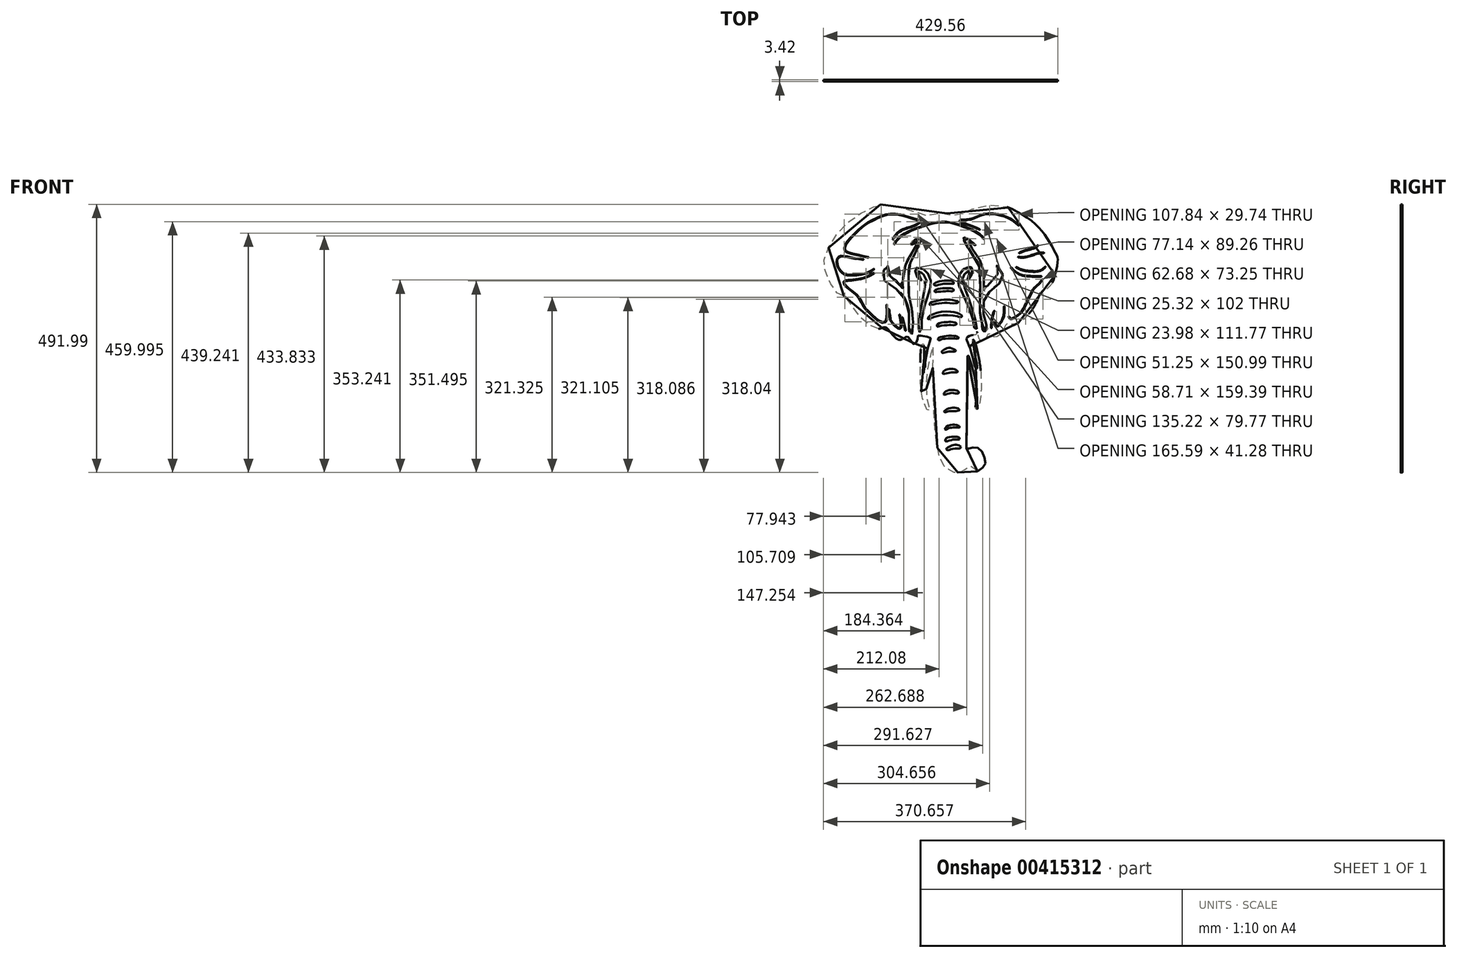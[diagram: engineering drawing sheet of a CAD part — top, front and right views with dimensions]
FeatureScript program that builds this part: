
annotation { "Feature Type Name" : "Feature", "Feature Type Description" : "" }
export const myFeature = defineFeature(function(context is Context, id is Id, definition is map)
    precondition{}
    {
        {
            var Q0;
            Q0=qCreatedBy(makeId("Front.planeOp"),FACE);
            var sketch = newSketch(context, id + "F0", { "sketchPlane" : qUnion([Q0])});
            skLineSegment(sketch, "E0.bottom", {"start": v(-254, 304.8) * mm, "end": v(254, 304.8) * mm, "construction": true});
            skLineSegment(sketch, "E0.top", {"start": v(-254, -304.8) * mm, "end": v(254, -304.8) * mm, "construction": true});
            skLineSegment(sketch, "E0.left", {"start": v(-254, 304.8) * mm, "end": v(-254, -304.8) * mm, "construction": true});
            skLineSegment(sketch, "E0.right", {"start": v(254, 304.8) * mm, "end": v(254, -304.8) * mm, "construction": true});
            skPoint(sketch, "E0.middle", {"position": v(0, 0) * mm});
            skFitSpline(sketch, "E1", {"points": [v(61.1, -298.65) * mm, v(58.43, -299.03) * mm, v(56.48, -297.46) * mm, v(55.38, -295.06) * mm, v(54.47, -292.78) * mm, v(53.43, -290.7) * mm, v(52.38, -289.33) * mm, v(49.59, -289.14) * mm, v(47.05, -290.05) * mm, v(44.58, -291.6) * mm, v(41, -293.95) * mm, v(37.1, -296.1) * mm, v(33.59, -297.79) * mm, v(31.57, -299.42) * mm, v(28.58, -300.46) * mm, v(24.8, -300.85) * mm, v(21.3, -300.85) * mm, v(18.56, -300.85) * mm, v(15.63, -299.35) * mm, v(12.77, -297.79) * mm, v(9.65, -295.9) * mm, v(6.07, -294.28) * mm, v(3.34, -292.46) * mm, v(1.71, -290.96) * mm, v(-1.44, -287.27) * mm, v(-6.48, -278.41) * mm, v(-10.96, -263.1) * mm, v(-13.8, -245.37) * mm, v(-15.64, -231.32) * mm, v(-18.25, -203.48) * mm, v(-19.03, -170.43) * mm, v(-20.63, -121.13) * mm, v(-20, -70.07) * mm, v(-20.33, -69.32) * mm, v(-21.37, -70.2) * mm, v(-22.67, -74.3) * mm, v(-26.44, -93.4) * mm, v(-30.85, -112.34) * mm, v(-33.09, -141.08) * mm, v(-32.47, -156.55) * mm, v(-30.92, -171.1) * mm, v(-26.28, -186.26) * mm, v(-26.21, -189.44) * mm, v(-27.85, -190.32) * mm, v(-29.93, -188.24) * mm, v(-32.77, -182.66) * mm, v(-39.01, -167.89) * mm, v(-42.3, -151.8) * mm, v(-43.94, -115.29) * mm, v(-43.16, -80.94) * mm, v(-40.04, -65.6) * mm, v(-37.95, -65.33) * mm, v(-36.91, -70.02) * mm, v(-36.91, -80.42) * mm, v(-36.91, -96.56) * mm, v(-37.95, -104.62) * mm, v(-39, -112.43) * mm, v(-39, -117.11) * mm, v(-37.7, -117.9) * mm, v(-36.4, -116.6) * mm, v(-36.65, -107.74) * mm, v(-35.1, -108.26) * mm, v(-34.83, -102.8) * mm, v(-33.27, -91.61) * mm, v(-29.63, -72.1) * mm, v(-24.95, -57.27) * mm, v(-24.72, -54.18) * mm, v(-29.1, -52.43) * mm, v(-43.32, -49.47) * mm, v(-47.15, -49.14) * mm, v(-48.57, -51.88) * mm, v(-48.46, -56.7) * mm, v(-50.54, -61.18) * mm, v(-54.04, -65.23) * mm, v(-56.77, -64.68) * mm, v(-61.15, -59.2) * mm, v(-65.75, -52.64) * mm, v(-67.28, -51) * mm, v(-70.34, -52.2) * mm, v(-76.36, -56.15) * mm, v(-81.39, -57.68) * mm, v(-87.19, -55.38) * mm, v(-99.63, -42.15) * mm, v(-106.13, -35.12) * mm, v(-110.56, -34.6) * mm, v(-114.72, -36.16) * mm, v(-122.53, -36.94) * mm, v(-131.9, -33.82) * mm, v(-142.3, -26.01) * mm, v(-158.7, -10.92) * mm, v(-168.06, 3.65) * mm, v(-177.17, 17.7) * mm, v(-186.8, 24.98) * mm, v(-195.12, 27.85) * mm, v(-203.19, 35.91) * mm, v(-213.07, 56.99) * mm, v(-220.44, 76.4) * mm, v(-220.48, 87.61) * mm, v(-213.98, 106.6) * mm, v(-202, 129.24) * mm, v(-183.01, 151.62) * mm, v(-160.12, 170.35) * mm, v(-139.04, 181.54) * mm, v(-121.87, 189.6) * mm, v(-109.38, 190.91) * mm, v(-91.16, 188.57) * mm, v(-61.72, 180.88) * mm, v(-34.4, 170.2) * mm, v(-28.41, 172.55) * mm, v(5.42, 174.11) * mm, v(15.82, 170.99) * mm, v(28.57, 174.11) * mm, v(37.42, 175.15) * mm, v(41.06, 178.53) * mm, v(73.07, 187.38) * mm, v(100.85, 190.41) * mm, v(157.08, 163.06) * mm, v(190.43, 126.35) * mm, v(206.4, 97.47) * mm, v(208.37, 87.84) * mm, v(199.26, 49.74) * mm, v(191.53, 38.91) * mm, v(185.03, 33.96) * mm, v(180.36, 33.27) * mm, v(175.16, 25.08) * mm, v(162.8, 0) * mm, v(138.7, -25.04) * mm, v(128.54, -28.94) * mm, v(119.96, -28.42) * mm, v(115.8, -27.38) * mm, v(109.81, -36.48) * mm, v(101.74, -48.71) * mm, v(92.12, -52.36) * mm, v(86.4, -48.45) * mm, v(81.19, -46.63) * mm, v(73.12, -59.9) * mm, v(68.18, -61.2) * mm, v(64.02, -55.22) * mm, v(61.67, -45.07) * mm, v(59.85, -43.25) * mm, v(58.81, -47.15) * mm, v(53.35, -48.71) * mm, v(45.8, -50.8) * mm, v(41.12, -53.92) * mm, v(42.94, -61.72) * mm, v(50.23, -81.24) * mm, v(58.62, -110.2) * mm, v(60.6, -109.77) * mm, v(57.97, -92.04) * mm, v(54.47, -72.57) * mm, v(52.72, -61.55) * mm, v(52.98, -57.13) * mm, v(57.01, -63.5) * mm, v(62.35, -84.45) * mm, v(66.39, -107.43) * mm, v(67.77, -129.06) * mm, v(66.78, -164.72) * mm, v(61.7, -183.07) * mm, v(59.63, -185.02) * mm, v(58.2, -184.5) * mm, v(57.55, -179.3) * mm, v(59.1, -163.03) * mm, v(58.07, -139.74) * mm, v(52.86, -111.51) * mm, v(43.37, -84.97) * mm, v(42.45, -91.22) * mm, v(42.98, -125.3) * mm, v(41.93, -179.55) * mm, v(41.15, -237.32) * mm, v(41.28, -257.35) * mm, v(42.2, -258.26) * mm, v(45.45, -256.83) * mm, v(51.7, -255.14) * mm, v(59.1, -254.75) * mm, v(67.56, -259.43) * mm, v(73.68, -272.05) * mm, v(75.63, -283.9) * mm, v(71.86, -290.66) * mm, v(61.1, -298.65) * mm]});
            skSolve(sketch);
        }
        {
            var Q0;
            Q0 = qSketchRegion(id + "F0", true);
            extrude(context, id + "F1", {"entities" : qUnion([Q0]), "endBound" : BoundingType.SYMMETRIC, "depth" : 3.42 * mm});
        }
        {
            var Q0;
            Q0=qCreatedBy(makeId("Front.planeOp"),FACE);
            var sketch = newSketch(context, id + "F2", { "sketchPlane" : qUnion([Q0])});
            skFitSpline(sketch, "E2", {"points": [v(30.41, -253.7) * mm, v(28.47, -251.76) * mm, v(21.82, -249.72) * mm, v(15.17, -250.74) * mm, v(7.8, -254.01) * mm, v(4.23, -257.39) * mm, v(5.45, -259.74) * mm, v(10.98, -258.62) * mm, v(22.23, -256.77) * mm, v(29.08, -256.47) * mm, v(30.41, -253.7) * mm]});
            skFitSpline(sketch, "E3", {"points": [v(28.06, -239.8) * mm, v(24.38, -240.3) * mm, v(16.4, -240.4) * mm, v(4.53, -243.68) * mm, v(2.18, -242.96) * mm, v(3, -239.08) * mm, v(11.8, -235.5) * mm, v(24.68, -235.4) * mm, v(27.45, -236.83) * mm, v(28.06, -239.8) * mm]});
            skFitSpline(sketch, "E4", {"points": [v(25.81, -218) * mm, v(15.48, -218.52) * mm, v(7.6, -220.05) * mm, v(2.9, -222.5) * mm, v(1.57, -220.15) * mm, v(13.23, -213.2) * mm, v(26.01, -214.83) * mm, v(28.06, -216.47) * mm, v(28.06, -218.41) * mm, v(25.81, -218) * mm]});
            skFitSpline(sketch, "E5", {"points": [v(14.66, -188.44) * mm, v(7.1, -188.65) * mm, v(2.38, -190.28) * mm, v(0, -189.36) * mm, v(1.67, -186.9) * mm, v(12.1, -182.4) * mm, v(24.48, -182.92) * mm, v(28.06, -186.2) * mm, v(25.81, -187.52) * mm, v(14.66, -188.44) * mm]});
            skFitSpline(sketch, "E6", {"points": [v(14.66, -154.79) * mm, v(6.78, -156.32) * mm, v(0, -158.06) * mm, v(-1, -156.52) * mm, v(1.67, -152.84) * mm, v(10.16, -149.47) * mm, v(19.37, -149.77) * mm, v(25.81, -152.02) * mm, v(26.73, -155) * mm, v(22.03, -155.8) * mm, v(14.66, -154.79) * mm]});
            skFitSpline(sketch, "E7", {"points": [v(10.57, -117.55) * mm, v(17.93, -117.04) * mm, v(23.25, -117.24) * mm, v(24.79, -115.6) * mm, v(21.1, -112.33) * mm, v(11.8, -110.8) * mm, v(4.33, -112.23) * mm, v(-1.7, -116.02) * mm, v(-2.42, -119.5) * mm, v(1.36, -119.9) * mm, v(10.57, -117.55) * mm]});
            skFitSpline(sketch, "E8", {"points": [v(8.32, -79.09) * mm, v(14.66, -78.98) * mm, v(19.88, -78.88) * mm, v(21.3, -77.25) * mm, v(17.83, -74.69) * mm, v(9.65, -72.13) * mm, v(2.49, -73.97) * mm, v(-2.22, -77.04) * mm, v(-4.37, -79.09) * mm, v(-3.24, -81.54) * mm, v(1.67, -80.52) * mm, v(8.32, -79.09) * mm]});
            skFitSpline(sketch, "E9", {"points": [v(6.99, -55.05) * mm, v(16.7, -54.74) * mm, v(23.97, -55.35) * mm, v(26.73, -53.82) * mm, v(23.46, -51.26) * mm, v(16.4, -50.14) * mm, v(4.02, -50.34) * mm, v(-3.65, -51.88) * mm, v(-10.5, -54.23) * mm, v(-11.22, -57.2) * mm, v(-8.36, -58.22) * mm, v(-4.06, -56.17) * mm, v(6.99, -55.05) * mm]});
            skFitSpline(sketch, "E10", {"points": [v(5.04, -30.5) * mm, v(13.43, -30.4) * mm, v(21.3, -29.98) * mm, v(22.84, -27.63) * mm, v(19.06, -25.69) * mm, v(9.95, -24.26) * mm, v(4.63, -25.18) * mm, v(-2.22, -25.18) * mm, v(-11.22, -28.45) * mm, v(-12.96, -29.68) * mm, v(-12.86, -33.36) * mm, v(-8.36, -32.24) * mm, v(5.04, -30.5) * mm]});
            skFitSpline(sketch, "E11", {"points": [v(-2.42, -12.6) * mm, v(-12.35, -13.82) * mm, v(-21.25, -16.17) * mm, v(-26.16, -19.14) * mm, v(-29.33, -19.55) * mm, v(-29.63, -16.69) * mm, v(-25.03, -12.8) * mm, v(-9.58, -6.76) * mm, v(12.4, -6.05) * mm, v(22.84, -8) * mm, v(30.41, -11.16) * mm, v(32.87, -14.33) * mm, v(30.41, -16.17) * mm, v(23.46, -14.13) * mm, v(-2.42, -12.6) * mm]});
            skFitSpline(sketch, "E12", {"points": [v(0.75, 10.32) * mm, v(10.06, 10.01) * mm, v(24.38, 10.32) * mm, v(25.81, 12.67) * mm, v(18.85, 14.72) * mm, v(9.55, 16.15) * mm, v(-4.26, 15.64) * mm, v(-18.18, 12.57) * mm, v(-26.05, 9.5) * mm, v(-26.57, 6.53) * mm, v(-21.25, 7.25) * mm, v(-10.5, 9.2) * mm, v(0.75, 10.32) * mm]});
            skFitSpline(sketch, "E13", {"points": [v(1.87, 31.59) * mm, v(9.27, 31.93) * mm, v(16.67, 31.93) * mm, v(17.61, 34.69) * mm, v(11.68, 37.18) * mm, v(4.2, 37.44) * mm, v(-7.33, 36.66) * mm, v(-15.76, 33.83) * mm, v(-17.48, 32.02) * mm, v(-16.7, 30.21) * mm, v(-9.83, 30.73) * mm, v(1.87, 31.59) * mm]});
            skFitSpline(sketch, "E14", {"points": [v(-3.9, 44.75) * mm, v(2.56, 45.52) * mm, v(12.7, 45.27) * mm, v(17.44, 45.78) * mm, v(16.92, 48.97) * mm, v(11.08, 51.12) * mm, v(1.78, 51.29) * mm, v(-9.05, 49.74) * mm, v(-16.97, 46.73) * mm, v(-18.86, 43.55) * mm, v(-16.1, 42.08) * mm, v(-9.48, 43.72) * mm, v(-3.9, 44.75) * mm]});
            skSolve(sketch);
        }
        {
            var Q0;
            Q0 = qSketchRegion(id + "F2", true);
            extrude(context, id + "F3", {"entities" : qUnion([Q0]), "operationType" : NewBodyOperationType.REMOVE, "endBound" : BoundingType.THROUGH_ALL, "oppositeDirection" : true, "depth" : 25.4 * mm, "hasSecondDirection" : true, "secondDirectionBound" : SecondDirectionBoundingType.THROUGH_ALL, "secondDirectionOppositeDirection" : false, "secondDirectionDepth" : 25.4 * mm});
        }
        {
            var Q0;
            Q0=qCreatedBy(makeId("Front.planeOp"),FACE);
            var sketch = newSketch(context, id + "F4", { "sketchPlane" : qUnion([Q0])});
            skFitSpline(sketch, "E15", {"points": [v(-47.27, 69.23) * mm, v(-42.4, 67.65) * mm, v(-36.57, 61.08) * mm, v(-33.28, 54.63) * mm, v(-31.95, 47.58) * mm, v(-32.43, 46.12) * mm, v(-35.47, 47.94) * mm, v(-36.81, 48.43) * mm, v(-37.3, 46.36) * mm, v(-34.99, 43.93) * mm, v(-34.5, 39.91) * mm, v(-36.94, 28.39) * mm, v(-41.18, 8.56) * mm, v(-44.8, -12.77) * mm, v(-46.69, -30.23) * mm, v(-46.52, -40.56) * mm, v(-44.2, -43.57) * mm, v(-41.61, -42.02) * mm, v(-41.1, -35.65) * mm, v(-40.92, -20.86) * mm, v(-34.9, 7.62) * mm, v(-30.52, 21.47) * mm, v(-25.76, 36.95) * mm, v(-24.73, 43.4) * mm, v(-24.9, 52.18) * mm, v(-28.08, 61.04) * mm, v(-30.66, 65.6) * mm, v(-35.91, 70.84) * mm, v(-41.85, 73.43) * mm, v(-50.02, 74.8) * mm, v(-53.2, 74.63) * mm, v(-53.46, 71.36) * mm, v(-52.08, 64.05) * mm, v(-49.76, 57.86) * mm, v(-46.15, 53.21) * mm, v(-42.45, 51.49) * mm, v(-41.76, 52.6) * mm, v(-42.97, 55.1) * mm, v(-45.12, 59.4) * mm, v(-47.27, 63.53) * mm, v(-47.27, 69.23) * mm]});
            skFitSpline(sketch, "E16", {"points": [v(-103.22, 76.95) * mm, v(-103.08, 64.3) * mm, v(-100.7, 61.08) * mm, v(-95.2, 56.77) * mm, v(-85.28, 48.09) * mm, v(-75.66, 36.59) * mm, v(-75.45, 39.48) * mm, v(-75.37, 57.13) * mm, v(-71.4, 77.38) * mm, v(-65.75, 90.55) * mm, v(-61.2, 98.43) * mm, v(-50.06, 117.1) * mm, v(-48.03, 121.36) * mm, v(-48.25, 122.74) * mm, v(-50.42, 122.74) * mm, v(-57.3, 118.18) * mm, v(-60.47, 117.38) * mm, v(-61.49, 118.4) * mm, v(-58.8, 122.6) * mm, v(-52.37, 127.44) * mm, v(-47.45, 129.97) * mm, v(-43.76, 129.97) * mm, v(-41.88, 127.37) * mm, v(-42.9, 122.66) * mm, v(-50.13, 108.13) * mm, v(-57.16, 95.55) * mm, v(-62.28, 83.17) * mm, v(-64.94, 70.69) * mm, v(-65.37, 53.14) * mm, v(-64.76, 22.49) * mm, v(-62.2, 10.93) * mm, v(-58.8, -1.48) * mm, v(-56.98, -11.82) * mm, v(-56.98, -32.99) * mm, v(-57.46, -42.84) * mm, v(-58.92, -46.49) * mm, v(-61.6, -46.85) * mm, v(-63.54, -43.45) * mm, v(-64.4, -36.51) * mm, v(-64.64, -16.8) * mm, v(-64.64, -4.4) * mm, v(-68.65, 10.2) * mm, v(-74.37, 22.6) * mm, v(-86.78, 34.9) * mm, v(-104.9, 46.82) * mm, v(-110.75, 52.54) * mm, v(-113.06, 59.96) * mm, v(-111.48, 68.6) * mm, v(-107.58, 77.35) * mm, v(-104.78, 80.03) * mm, v(-103.22, 76.95) * mm]});
            skFitSpline(sketch, "E17", {"points": [v(28.9, 62.27) * mm, v(33.29, 70.18) * mm, v(38.28, 73.22) * mm, v(44.36, 75.41) * mm, v(49.83, 75.41) * mm, v(51.17, 71.76) * mm, v(51.17, 65.68) * mm, v(48.25, 58.14) * mm, v(44.48, 53.15) * mm, v(42.9, 52.54) * mm, v(42.9, 55.34) * mm, v(45.57, 62.76) * mm, v(47.4, 66.9) * mm, v(46.3, 69.08) * mm, v(43.02, 68.36) * mm, v(38.28, 65.07) * mm, v(35.48, 58.26) * mm, v(32.92, 52.05) * mm, v(33.17, 46.82) * mm, v(35, 45.73) * mm, v(36.7, 47.67) * mm, v(38.76, 47.43) * mm, v(38.03, 44.51) * mm, v(37.42, 39.04) * mm, v(40.47, 30.64) * mm, v(46.55, 13.73) * mm, v(52.02, -2.69) * mm, v(58.47, -24.46) * mm, v(59.93, -36.75) * mm, v(58.23, -37.72) * mm, v(56.28, -37.48) * mm, v(54.46, -32.25) * mm, v(52.14, -18.87) * mm, v(45.82, 0) * mm, v(37.79, 18.84) * mm, v(27.81, 40.86) * mm, v(26.6, 44.15) * mm, v(26.6, 52.9) * mm, v(28.9, 62.27) * mm]});
            skFitSpline(sketch, "E18", {"points": [v(44.88, 127.77) * mm, v(55.7, 119.26) * mm, v(58.26, 116.83) * mm, v(57.17, 115.85) * mm, v(55.1, 116.58) * mm, v(48.29, 120.72) * mm, v(44.52, 123.15) * mm, v(43.66, 121.57) * mm, v(46.7, 115.85) * mm, v(55.95, 103.57) * mm, v(65.32, 89.45) * mm, v(69.82, 79) * mm, v(72.98, 67.2) * mm, v(74.08, 51.13) * mm, v(72.5, 32.89) * mm, v(73.83, 32.89) * mm, v(79.19, 41.52) * mm, v(97.31, 61.08) * mm, v(97.8, 64.15) * mm, v(96.1, 75.22) * mm, v(96.1, 78.75) * mm, v(98.53, 78.14) * mm, v(105.7, 66.22) * mm, v(108.02, 57.46) * mm, v(105.46, 49.07) * mm, v(97.68, 44.32) * mm, v(86.6, 34.95) * mm, v(76.15, 22.67) * mm, v(73.23, 17.56) * mm, v(72, 7.34) * mm, v(71.89, -6.77) * mm, v(73.96, -23.92) * mm, v(77.48, -30.13) * mm, v(79.67, -34.5) * mm, v(78.46, -40.47) * mm, v(73.35, -42.05) * mm, v(70.18, -39.25) * mm, v(69.58, -29.4) * mm, v(68.36, -22.47) * mm, v(66.05, -11.4) * mm, v(65.93, 31.55) * mm, v(64.59, 74.61) * mm, v(60.45, 86.05) * mm, v(47.44, 105.63) * mm, v(37.46, 122.79) * mm, v(35.51, 129.23) * mm, v(37.95, 130.57) * mm, v(44.88, 127.77) * mm]});
            skSolve(sketch);
        }
        {
            var Q0;
            Q0 = qSketchRegion(id + "F4", true);
            extrude(context, id + "F5", {"entities" : qUnion([Q0]), "operationType" : NewBodyOperationType.REMOVE, "endBound" : BoundingType.THROUGH_ALL, "oppositeDirection" : true, "depth" : 25.4 * mm, "hasSecondDirection" : true, "secondDirectionBound" : SecondDirectionBoundingType.THROUGH_ALL, "secondDirectionOppositeDirection" : false, "secondDirectionDepth" : 25.4 * mm});
        }
        {
            var Q0;
            Q0=qCreatedBy(makeId("Front.planeOp"),FACE);
            var sketch = newSketch(context, id + "F6", { "sketchPlane" : qUnion([Q0])});
            skFitSpline(sketch, "E19", {"points": [v(-71.36, -40.3) * mm, v(-77.15, -17) * mm], "startDerivative": vector(-5.79, 23.3) * mm, "endDerivative": vector(-5.79, 23.3) * mm});
            skFitSpline(sketch, "E20", {"points": [v(-82.28, -11.87) * mm, v(-81.56, -35.95) * mm, v(-96.6, -23.15) * mm, v(-98.5, -17.07) * mm, v(-100.97, -1.72) * mm], "startDerivative": vector(22.12, -113.85) * mm, "endDerivative": vector(-12.6, 71.3) * mm});
            skFitSpline(sketch, "E21", {"points": [v(-105.88, 6.26) * mm, v(-106.08, -19.32) * mm, v(-108.94, -24.64) * mm, v(-117.54, -23.82) * mm, v(-139.02, -4.59) * mm, v(-145.98, 2.57) * mm, v(-155.18, 19.76) * mm, v(-167.87, 31.63) * mm, v(-179.32, 41.24) * mm, v(-183.21, 46.36) * mm, v(-183, 49.42) * mm, v(-178.1, 50.65) * mm, v(-168.89, 51.47) * mm, v(-155.8, 53.1) * mm, v(-142.5, 57) * mm, v(-128.58, 63.75) * mm], "startDerivative": vector(12.16, -310.07) * mm, "endDerivative": vector(185.2, 97.32) * mm});
            skFitSpline(sketch, "E22", {"points": [v(-128.58, 71.52) * mm, v(-136.97, 66.4) * mm, v(-155.39, 61.09) * mm, v(-171.75, 60.47) * mm, v(-180.55, 61.09) * mm, v(-187.92, 65.8) * mm, v(-194.46, 74.18) * mm, v(-197.33, 87.68) * mm, v(-192.42, 95.46) * mm, v(-183.42, 96.48) * mm, v(-168.28, 93.41) * mm, v(-148.63, 90.75) * mm], "startDerivative": vector(-90.9, -64.53) * mm, "endDerivative": vector(175.67, -19.14) * mm});
            skFitSpline(sketch, "E23", {"points": [v(-139.02, 94.23) * mm, v(-159.89, 99.14) * mm, v(-176.46, 103.44) * mm, v(-181.17, 106.71) * mm, v(-181.17, 113.87) * mm, v(-175.64, 123.28) * mm, v(-161.73, 138.42) * mm, v(-142.7, 154.59) * mm, v(-122.86, 165.02) * mm, v(-107.1, 170.95) * mm, v(-89.5, 172.59) * mm, v(-70.9, 168.5) * mm, v(-48.59, 161.54) * mm], "startDerivative": vector(-219.91, 52.2) * mm, "endDerivative": vector(230.65, -73.26) * mm});
            skFitSpline(sketch, "E24", {"points": [v(-43.27, 157.65) * mm, v(-57.39, 150.08) * mm, v(-74.57, 144.36) * mm, v(-87.26, 135.56) * mm, v(-92.99, 126.76) * mm], "startDerivative": vector(-51.9, -32.23) * mm, "endDerivative": vector(-22.7, -42.68) * mm});
            skFitSpline(sketch, "E25", {"points": [v(-91.76, 118.58) * mm, v(-85.21, 127.78) * mm, v(-69.05, 139.45) * mm, v(-41.22, 150.9) * mm, v(-18.72, 157.45) * mm, v(5.42, 159.09) * mm, v(25.68, 154.38) * mm, v(45.93, 147.02) * mm, v(66.6, 135.56) * mm, v(73.55, 128.2) * mm], "startDerivative": vector(66.6, 110.8) * mm, "endDerivative": vector(70.46, -91.26) * mm});
            skFitSpline(sketch, "E26", {"points": [v(65.37, 145.38) * mm, v(49.61, 152.33) * mm, v(32.84, 158.06) * mm, v(29.36, 160.52) * mm, v(34.88, 161.95) * mm, v(48.6, 162.97) * mm, v(63.53, 168.9) * mm, v(78.46, 173) * mm, v(97.7, 171.77) * mm, v(119.79, 164.61) * mm, v(136.36, 152.33) * mm], "startDerivative": vector(-138.06, 67.12) * mm, "endDerivative": vector(129.97, -112.95) * mm});
            skFitSpline(sketch, "E27", {"points": [v(138.16, 101.18) * mm, v(150.08, 106.05) * mm, v(163.95, 109.94) * mm, v(172.22, 114.8) * mm], "startDerivative": vector(33.17, 15.53) * mm, "endDerivative": vector(25.28, 18.06) * mm});
            skFitSpline(sketch, "E28", {"points": [v(136.36, 94.86) * mm, v(146.92, 94.62) * mm, v(162.98, 99) * mm, v(174.66, 102.4) * mm, v(182.69, 102.64) * mm], "startDerivative": vector(41.67, -4.66) * mm, "endDerivative": vector(37.62, -1.41) * mm});
            skFitSpline(sketch, "E29", {"points": [v(132.32, 74.9) * mm, v(142.78, 70.04) * mm, v(158.6, 67.6) * mm, v(175.87, 68.58) * mm, v(185.85, 75.64) * mm], "startDerivative": vector(43.65, -24.28) * mm, "endDerivative": vector(38.17, 36.38) * mm});
            skFitSpline(sketch, "E30", {"points": [v(122.6, 73.93) * mm, v(129.65, 67.37) * mm, v(141.81, 60.8) * mm, v(161.52, 58.36) * mm, v(177.82, 58.36) * mm], "startDerivative": vector(32.22, -32.72) * mm, "endDerivative": vector(59.32, 0.86) * mm});
            skFitSpline(sketch, "E31", {"points": [v(179.77, 53.5) * mm, v(175.14, 47.42) * mm, v(170.52, 43.04) * mm, v(163.95, 36.7) * mm, v(156.65, 23.57) * mm, v(151.79, 13.84) * mm, v(141.57, -5.62) * mm, v(128.67, -15.84) * mm, v(121.62, -18.28) * mm, v(119.43, -14.87) * mm], "startDerivative": vector(-47.91, -67.49) * mm, "endDerivative": vector(-22.85, 64.4) * mm});
            skFitSpline(sketch, "E32", {"points": [v(109.7, 3.62) * mm, v(108.72, -12.68) * mm, v(105.32, -21.68) * mm, v(96.8, -31.9) * mm, v(93.64, -24.36) * mm], "startDerivative": vector(-1.4, -61.13) * mm, "endDerivative": vector(-10.12, 53.87) * mm});
            skFitSpline(sketch, "E33", {"points": [v(91.3, -4.65) * mm, v(87.6, -16.31) * mm, v(85.97, -35.34) * mm], "startDerivative": vector(-9.47, -24.45) * mm, "endDerivative": vector(-1.46, -36.48) * mm});
            skFitSpline(sketch, "E34.0", {"points": [v(-139.31, 93) * mm, v(-141.6, 93.54) * mm, v(-146.18, 94.63) * mm, v(-153.07, 96.25) * mm, v(-158.81, 97.6) * mm, v(-163.44, 98.66) * mm, v(-166.84, 99.45) * mm, v(-170.1, 100.25) * mm, v(-173.1, 101.05) * mm, v(-175.36, 101.72) * mm, v(-176.96, 102.26) * mm, v(-178.44, 102.82) * mm, v(-179.75, 103.45) * mm, v(-180.89, 104.28) * mm, v(-181.63, 105.03) * mm, v(-182.13, 105.78) * mm, v(-182.45, 106.44) * mm, v(-182.7, 107.13) * mm, v(-182.92, 108.03) * mm, v(-183.1, 109.55) * mm, v(-183.01, 111.55) * mm, v(-182.6, 113.59) * mm, v(-182.1, 115.17) * mm, v(-181.48, 116.72) * mm, v(-180.52, 118.6) * mm, v(-179.1, 120.82) * mm, v(-177.45, 123.07) * mm, v(-175.57, 125.4) * mm, v(-173.48, 127.86) * mm, v(-171.21, 130.4) * mm, v(-167.99, 133.89) * mm, v(-164.5, 137.46) * mm, v(-160.9, 141.04) * mm, v(-157.2, 144.59) * mm, v(-153.35, 148.05) * mm, v(-149.35, 151.34) * mm, v(-146.27, 153.68) * mm, v(-143.1, 155.89) * mm, v(-139.84, 157.92) * mm, v(-136.55, 159.8) * mm, v(-133.26, 161.53) * mm, v(-129.99, 163.14) * mm, v(-126.77, 164.65) * mm, v(-123.65, 166.06) * mm, v(-120.64, 167.4) * mm, v(-117.7, 168.66) * mm, v(-114.78, 169.83) * mm, v(-111.85, 170.9) * mm, v(-108.86, 171.82) * mm, v(-105.76, 172.61) * mm, v(-102.56, 173.24) * mm, v(-99.3, 173.7) * mm, v(-95.97, 173.97) * mm, v(-92.63, 174.03) * mm, v(-89.28, 173.88) * mm, v(-85.97, 173.5) * mm, v(-81.6, 172.74) * mm, v(-77.23, 171.66) * mm, v(-72.8, 170.4) * mm, v(-68.32, 169.05) * mm, v(-62.53, 167.28) * mm, v(-55.41, 165.04) * mm, v(-50.6, 163.51) * mm, v(-48.2, 162.75) * mm]});
            skFitSpline(sketch, "E35.0", {"points": [v(-43.94, 158.73) * mm, v(-45.02, 158.06) * mm, v(-47.18, 156.72) * mm, v(-50.44, 154.8) * mm, v(-53.23, 153.31) * mm, v(-55.53, 152.23) * mm, v(-57.3, 151.47) * mm, v(-59.11, 150.78) * mm, v(-61.63, 149.93) * mm, v(-64.89, 148.96) * mm, v(-68.22, 147.98) * mm, v(-70.89, 147.12) * mm, v(-72.87, 146.42) * mm, v(-74.83, 145.64) * mm, v(-77.38, 144.49) * mm, v(-80.41, 142.83) * mm, v(-83.73, 140.57) * mm, v(-86.16, 138.5) * mm, v(-87.88, 136.78) * mm, v(-89.43, 135.01) * mm, v(-91.06, 132.76) * mm, v(-92.68, 130.04) * mm, v(-93.63, 128.25) * mm, v(-94.1, 127.36) * mm]});
            skFitSpline(sketch, "E36.0", {"points": [v(64.81, 144.24) * mm, v(63.37, 144.94) * mm, v(60.5, 146.33) * mm, v(56.85, 148.03) * mm, v(53.82, 149.33) * mm, v(51.48, 150.28) * mm, v(49.07, 151.2) * mm, v(46.56, 152.07) * mm, v(44, 152.9) * mm, v(41.45, 153.73) * mm, v(38.95, 154.53) * mm, v(36.56, 155.31) * mm, v(34.7, 155.97) * mm, v(33.32, 156.5) * mm, v(32.34, 156.9) * mm, v(31.42, 157.3) * mm, v(30.58, 157.7) * mm, v(29.83, 158.12) * mm, v(29.28, 158.48) * mm, v(28.9, 158.8) * mm, v(28.62, 159.07) * mm, v(28.37, 159.39) * mm, v(28.16, 159.8) * mm, v(28.06, 160.26) * mm, v(28.09, 160.67) * mm, v(28.16, 160.97) * mm, v(28.28, 161.23) * mm, v(28.48, 161.53) * mm, v(28.75, 161.8) * mm, v(29.08, 162.03) * mm, v(29.42, 162.21) * mm, v(29.77, 162.36) * mm, v(30.27, 162.53) * mm, v(30.94, 162.7) * mm, v(31.83, 162.88) * mm, v(32.8, 163.03) * mm, v(33.82, 163.14) * mm, v(34.88, 163.23) * mm, v(36.3, 163.31) * mm, v(38.11, 163.37) * mm, v(40.3, 163.41) * mm, v(42.5, 163.49) * mm, v(44.7, 163.64) * mm, v(46.52, 163.86) * mm, v(47.96, 164.13) * mm, v(49.39, 164.46) * mm, v(51.19, 165) * mm, v(53.36, 165.79) * mm, v(55.55, 166.7) * mm, v(57.74, 167.69) * mm, v(59.95, 168.7) * mm, v(62.18, 169.72) * mm, v(64.41, 170.67) * mm, v(67.4, 171.82) * mm, v(71.2, 173.02) * mm, v(75.13, 173.87) * mm, v(78.4, 174.3) * mm, v(81.74, 174.54) * mm, v(86.06, 174.53) * mm, v(91.44, 174.07) * mm, v(96.07, 173.38) * mm, v(99.84, 172.66) * mm, v(103.65, 171.84) * mm, v(108.44, 170.58) * mm, v(113.13, 169) * mm, v(116.76, 167.5) * mm, v(119.4, 166.27) * mm, v(121.92, 164.91) * mm, v(125.13, 162.95) * mm, v(128.9, 160.28) * mm, v(133.12, 156.83) * mm, v(135.84, 154.47) * mm, v(137.2, 153.3) * mm]});
            skFitSpline(sketch, "E37.0", {"points": [v(137.62, 102.33) * mm, v(139, 102.98) * mm, v(141.1, 103.96) * mm, v(143.98, 105.2) * mm, v(146.21, 106.1) * mm, v(148.54, 106.92) * mm, v(151, 107.65) * mm, v(153.5, 108.3) * mm, v(156, 108.92) * mm, v(158.46, 109.54) * mm, v(160.8, 110.18) * mm, v(162.98, 110.9) * mm, v(164.9, 111.71) * mm, v(166.67, 112.64) * mm, v(168.33, 113.64) * mm, v(169.91, 114.72) * mm, v(170.96, 115.47) * mm, v(171.49, 115.84) * mm]});
            skFitSpline(sketch, "E38.0", {"points": [v(136.22, 93.6) * mm, v(137.09, 93.5) * mm, v(138.84, 93.3) * mm, v(141.59, 93.1) * mm, v(144.02, 93.1) * mm, v(146.08, 93.23) * mm, v(147.7, 93.43) * mm, v(149.36, 93.7) * mm, v(151.62, 94.18) * mm, v(154.53, 94.93) * mm, v(158.04, 96) * mm, v(160.9, 96.94) * mm, v(163.1, 97.7) * mm, v(165.24, 98.43) * mm, v(167.76, 99.3) * mm, v(170.58, 100.18) * mm, v(172.77, 100.76) * mm, v(174.43, 101.09) * mm, v(176.03, 101.32) * mm, v(177.99, 101.46) * mm, v(180.3, 101.46) * mm, v(181.86, 101.4) * mm, v(182.64, 101.38) * mm]});
            skFitSpline(sketch, "E39.0", {"points": [v(132.94, 76.02) * mm, v(133.85, 75.51) * mm, v(135.66, 74.5) * mm, v(138.4, 73.1) * mm, v(140.8, 72.06) * mm, v(142.8, 71.35) * mm, v(144.9, 70.73) * mm, v(147.73, 70.1) * mm, v(151.36, 69.55) * mm, v(154.57, 69.2) * mm, v(157.22, 68.99) * mm, v(159.25, 68.83) * mm, v(161.3, 68.7) * mm, v(164.03, 68.56) * mm, v(167.4, 68.5) * mm, v(171.21, 68.75) * mm, v(174.09, 69.3) * mm, v(176.12, 70) * mm, v(178, 70.88) * mm, v(180.18, 72.27) * mm, v(182.6, 74.3) * mm, v(184.18, 75.8) * mm, v(184.97, 76.56) * mm]});
            skFitSpline(sketch, "E40.0", {"points": [v(123.5, 74.83) * mm, v(124.17, 74.14) * mm, v(125.5, 72.79) * mm, v(127.57, 70.79) * mm, v(129.8, 68.83) * mm, v(132.3, 66.9) * mm, v(135.1, 65.08) * mm, v(137.7, 63.72) * mm, v(139.94, 62.77) * mm, v(141.7, 62.14) * mm, v(143.57, 61.6) * mm, v(146.18, 60.99) * mm, v(149.63, 60.41) * mm, v(153.93, 59.97) * mm, v(158.26, 59.72) * mm, v(162.49, 59.6) * mm, v(166.5, 59.54) * mm, v(171.63, 59.54) * mm, v(175.33, 59.6) * mm, v(177.8, 59.63) * mm]});
            skFitSpline(sketch, "E41.0", {"points": [v(180.8, 52.76) * mm, v(180.3, 52.06) * mm, v(179.3, 50.65) * mm, v(178.02, 48.92) * mm, v(176.98, 47.61) * mm, v(176.19, 46.66) * mm, v(175.38, 45.77) * mm, v(174.28, 44.65) * mm, v(173.15, 43.6) * mm, v(171.96, 42.58) * mm, v(171.04, 41.81) * mm, v(170.09, 41.04) * mm, v(168.8, 39.98) * mm, v(167.5, 38.82) * mm, v(166.23, 37.49) * mm, v(165.44, 36.57) * mm, v(164.82, 35.76) * mm, v(164.2, 34.91) * mm, v(163.45, 33.76) * mm, v(162.55, 32.27) * mm, v(161.38, 30.19) * mm, v(160.27, 28.02) * mm, v(159.21, 25.89) * mm, v(158.45, 24.34) * mm, v(157.72, 22.86) * mm, v(157.03, 21.5) * mm, v(156.37, 20.22) * mm, v(155.5, 18.56) * mm, v(154.66, 16.9) * mm, v(153.78, 15.1) * mm, v(153.1, 13.65) * mm, v(152.36, 12.03) * mm, v(151.33, 9.68) * mm, v(149.9, 6.45) * mm, v(147.97, 2.36) * mm, v(146.17, -1.03) * mm, v(144.58, -3.6) * mm, v(143.32, -5.45) * mm, v(141.98, -7.18) * mm, v(140.57, -8.74) * mm, v(139.1, -10.17) * mm, v(137.11, -11.9) * mm, v(135.07, -13.42) * mm, v(133.04, -14.75) * mm, v(131.53, -15.67) * mm, v(130.04, -16.53) * mm, v(128.6, -17.34) * mm, v(127.19, -18.11) * mm, v(125.82, -18.79) * mm, v(124.5, -19.32) * mm, v(123.42, -19.6) * mm, v(122.56, -19.7) * mm, v(122.01, -19.67) * mm, v(121.57, -19.6) * mm, v(121.24, -19.5) * mm, v(120.92, -19.37) * mm, v(120.53, -19.15) * mm, v(120.1, -18.82) * mm, v(119.54, -18.2) * mm, v(119.04, -17.37) * mm, v(118.6, -16.32) * mm, v(118.35, -15.63) * mm, v(118.23, -15.3) * mm]});
            skFitSpline(sketch, "E42.0", {"points": [v(110.97, 3.6) * mm, v(110.94, 2.32) * mm, v(110.88, -0.23) * mm, v(110.76, -3.97) * mm, v(110.58, -7.52) * mm, v(110.34, -10.24) * mm, v(110.09, -12.23) * mm, v(109.86, -13.62) * mm, v(109.58, -14.92) * mm, v(109.12, -16.58) * mm, v(108.52, -18.19) * mm, v(107.73, -19.87) * mm, v(107.04, -21.21) * mm, v(106.23, -22.67) * mm, v(105.3, -24.26) * mm, v(104.27, -25.92) * mm, v(103.17, -27.57) * mm, v(102.05, -29.13) * mm, v(100.9, -30.55) * mm, v(99.95, -31.54) * mm, v(99.18, -32.2) * mm, v(98.6, -32.62) * mm, v(97.96, -32.95) * mm, v(97.38, -33.13) * mm, v(96.86, -33.18) * mm, v(96.33, -33.15) * mm, v(95.7, -32.94) * mm, v(95.09, -32.52) * mm, v(94.63, -32) * mm, v(94.26, -31.44) * mm, v(93.86, -30.61) * mm, v(93.45, -29.47) * mm, v(93.05, -27.93) * mm, v(92.7, -26.28) * mm, v(92.5, -25.15) * mm, v(92.39, -24.6) * mm]});
            skFitSpline(sketch, "E43.0", {"points": [v(92.47, -5.11) * mm, v(92.08, -6.13) * mm, v(91.3, -8.16) * mm, v(90.2, -11.26) * mm, v(89.41, -14) * mm, v(88.88, -16.34) * mm, v(88.55, -18.2) * mm, v(88.26, -20.14) * mm, v(87.95, -22.84) * mm, v(87.66, -26.39) * mm, v(87.42, -30.84) * mm, v(87.3, -33.87) * mm, v(87.24, -35.4) * mm]});
            skFitSpline(sketch, "E44.0", {"points": [v(-70.13, -39.99) * mm, v(-72.06, -32.22) * mm, v(-73.98, -24.46) * mm, v(-75.91, -16.7) * mm]});
            skFitSpline(sketch, "E45.0", {"points": [v(-81.04, -11.63) * mm, v(-80.57, -14) * mm, v(-79.88, -17.56) * mm, v(-79.1, -22.06) * mm, v(-78.63, -25.24) * mm, v(-78.31, -28.17) * mm, v(-78.18, -30.79) * mm, v(-78.26, -32.67) * mm, v(-78.49, -34) * mm, v(-78.75, -34.92) * mm, v(-79.15, -35.75) * mm, v(-79.73, -36.48) * mm, v(-80.41, -36.94) * mm, v(-81.03, -37.16) * mm, v(-81.52, -37.24) * mm, v(-82, -37.25) * mm, v(-82.63, -37.19) * mm, v(-83.4, -36.99) * mm, v(-84.33, -36.6) * mm, v(-85.6, -35.94) * mm, v(-87.22, -34.83) * mm, v(-89.25, -33.19) * mm, v(-91.28, -31.32) * mm, v(-93.23, -29.33) * mm, v(-95.02, -27.32) * mm, v(-96.57, -25.4) * mm, v(-97.81, -23.68) * mm, v(-98.67, -22.2) * mm, v(-99.21, -20.88) * mm, v(-99.51, -19.63) * mm, v(-99.63, -18.65) * mm, v(-99.7, -17.86) * mm, v(-99.77, -17.24) * mm, v(-99.84, -16.58) * mm, v(-99.96, -15.6) * mm, v(-100.14, -14.27) * mm, v(-100.41, -12.49) * mm, v(-100.83, -9.91) * mm, v(-101.43, -6.4) * mm, v(-101.95, -3.43) * mm, v(-102.22, -1.94) * mm]});
            skFitSpline(sketch, "E46.0", {"points": [v(-104.6, 6.3) * mm, v(-104.48, 3.08) * mm, v(-104.29, -1.78) * mm, v(-104.17, -7.82) * mm, v(-104.2, -12.03) * mm, v(-104.36, -15.82) * mm, v(-104.7, -19.09) * mm, v(-105.18, -21.31) * mm, v(-105.75, -22.85) * mm, v(-106.31, -23.88) * mm, v(-107.03, -24.77) * mm, v(-107.9, -25.52) * mm, v(-108.9, -26.08) * mm, v(-110.42, -26.6) * mm, v(-112.16, -26.76) * mm, v(-114.07, -26.5) * mm, v(-115.58, -26.09) * mm, v(-117.17, -25.46) * mm, v(-118.82, -24.59) * mm, v(-120.52, -23.5) * mm, v(-122.85, -21.8) * mm, v(-125.83, -19.32) * mm, v(-129.42, -15.96) * mm, v(-132.91, -12.5) * mm, v(-135.63, -9.74) * mm, v(-137.62, -7.73) * mm, v(-138.77, -6.6) * mm, v(-139.62, -5.77) * mm, v(-140.43, -5) * mm, v(-141.36, -4.15) * mm, v(-142.38, -3.24) * mm, v(-143.64, -2.12) * mm, v(-145.08, -0.74) * mm, v(-146.42, 0.9) * mm, v(-147.47, 2.54) * mm, v(-148.5, 4.37) * mm, v(-149.78, 6.95) * mm, v(-151.4, 10.34) * mm, v(-152.82, 13.24) * mm, v(-154.02, 15.5) * mm, v(-154.97, 17.12) * mm, v(-155.95, 18.66) * mm, v(-156.97, 20.09) * mm, v(-158.05, 21.41) * mm, v(-159.54, 23.08) * mm, v(-161.52, 24.98) * mm, v(-164.04, 27.09) * mm, v(-166.22, 28.77) * mm, v(-168, 30.13) * mm, v(-169.81, 31.52) * mm, v(-172.06, 33.29) * mm, v(-174.67, 35.41) * mm, v(-177.12, 37.5) * mm, v(-178.96, 39.14) * mm, v(-180.28, 40.4) * mm, v(-181.5, 41.6) * mm, v(-182.55, 42.76) * mm, v(-183.4, 43.94) * mm, v(-183.95, 44.85) * mm, v(-184.38, 45.8) * mm, v(-184.68, 46.78) * mm, v(-184.82, 47.8) * mm, v(-184.75, 48.68) * mm, v(-184.53, 49.38) * mm, v(-184.31, 49.8) * mm, v(-184.09, 50.12) * mm, v(-183.82, 50.42) * mm, v(-183.46, 50.73) * mm, v(-182.98, 51.02) * mm, v(-182.32, 51.3) * mm, v(-181.47, 51.55) * mm, v(-180.38, 51.72) * mm, v(-179.45, 51.82) * mm, v(-178.69, 51.88) * mm, v(-177.93, 51.94) * mm, v(-176.98, 52.02) * mm, v(-175.82, 52.12) * mm, v(-174.22, 52.26) * mm, v(-172.16, 52.44) * mm, v(-169.54, 52.69) * mm, v(-166.76, 52.94) * mm, v(-163.86, 53.24) * mm, v(-160.89, 53.58) * mm, v(-157.9, 54.01) * mm, v(-154.94, 54.55) * mm, v(-152.04, 55.2) * mm, v(-149.18, 55.98) * mm, v(-146.34, 56.89) * mm, v(-143.5, 57.93) * mm, v(-140.67, 59.13) * mm, v(-137.81, 60.45) * mm, v(-133.99, 62.34) * mm, v(-131.1, 63.86) * mm, v(-129.18, 64.87) * mm]});
            skFitSpline(sketch, "E47.0", {"points": [v(-129.32, 72.56) * mm, v(-130.27, 71.88) * mm, v(-131.67, 70.89) * mm, v(-133.7, 69.6) * mm, v(-135.34, 68.64) * mm, v(-137.16, 67.7) * mm, v(-139.22, 66.77) * mm, v(-141.5, 65.88) * mm, v(-144.77, 64.74) * mm, v(-149.16, 63.49) * mm, v(-153.7, 62.58) * mm, v(-157.25, 62.12) * mm, v(-159.87, 61.9) * mm, v(-162.42, 61.79) * mm, v(-164.9, 61.74) * mm, v(-167.29, 61.73) * mm, v(-169.19, 61.75) * mm, v(-170.65, 61.75) * mm, v(-171.72, 61.74) * mm, v(-172.75, 61.73) * mm, v(-174.06, 61.71) * mm, v(-175.6, 61.7) * mm, v(-177.3, 61.76) * mm, v(-178.59, 61.91) * mm, v(-179.58, 62.12) * mm, v(-180.3, 62.33) * mm, v(-181.02, 62.6) * mm, v(-181.98, 63.02) * mm, v(-183.18, 63.69) * mm, v(-184.6, 64.66) * mm, v(-186, 65.78) * mm, v(-187.37, 67) * mm, v(-188.68, 68.28) * mm, v(-189.93, 69.64) * mm, v(-191.1, 71.1) * mm, v(-192.2, 72.7) * mm, v(-193.2, 74.45) * mm, v(-194.13, 76.4) * mm, v(-195.21, 79.2) * mm, v(-195.96, 82.15) * mm, v(-196.24, 85) * mm, v(-196.2, 86.7) * mm, v(-196, 87.95) * mm, v(-195.73, 89.16) * mm, v(-195.2, 90.56) * mm, v(-194.35, 92.03) * mm, v(-193.3, 93.26) * mm, v(-192.12, 94.21) * mm, v(-190.82, 94.87) * mm, v(-189.36, 95.28) * mm, v(-187.74, 95.47) * mm, v(-185.95, 95.47) * mm, v(-184.01, 95.3) * mm, v(-181.95, 95) * mm, v(-179.07, 94.46) * mm, v(-176, 93.77) * mm, v(-172.75, 93.04) * mm, v(-170.25, 92.5) * mm, v(-167.68, 92) * mm, v(-165.06, 91.54) * mm, v(-162.4, 91.13) * mm, v(-158.81, 90.64) * mm, v(-154.27, 90.09) * mm, v(-150.6, 89.69) * mm, v(-148.77, 89.49) * mm]});
            skFitSpline(sketch, "E48.0", {"points": [v(-90.67, 117.92) * mm, v(-89.98, 119.08) * mm, v(-88.6, 121.36) * mm, v(-86.66, 124.15) * mm, v(-84.82, 126.36) * mm, v(-83.25, 128.02) * mm, v(-81.46, 129.67) * mm, v(-78.81, 131.87) * mm, v(-75.02, 134.57) * mm, v(-70.63, 137.19) * mm, v(-66.8, 139.2) * mm, v(-62.77, 141.15) * mm, v(-57.45, 143.48) * mm, v(-51.97, 145.64) * mm, v(-47.6, 147.28) * mm, v(-44.36, 148.45) * mm, v(-41.2, 149.57) * mm, v(-38.13, 150.64) * mm, v(-35.17, 151.64) * mm, v(-31.3, 152.9) * mm, v(-27.52, 154.03) * mm, v(-23.74, 155.03) * mm, v(-20.86, 155.71) * mm, v(-17.94, 156.32) * mm, v(-14.93, 156.86) * mm, v(-11.88, 157.31) * mm, v(-7.76, 157.8) * mm, v(-3.62, 158.07) * mm, v(0.46, 158.1) * mm, v(3.48, 157.99) * mm, v(6.41, 157.73) * mm, v(10.24, 157.2) * mm, v(14.88, 156.24) * mm, v(19.4, 155) * mm, v(22.98, 153.9) * mm, v(25.66, 153.05) * mm, v(28.34, 152.2) * mm, v(31.9, 151.03) * mm, v(35.48, 149.8) * mm, v(39.13, 148.43) * mm, v(41.9, 147.34) * mm, v(44.75, 146.16) * mm, v(47.66, 144.87) * mm, v(50.6, 143.5) * mm, v(54.5, 141.57) * mm, v(58.25, 139.55) * mm, v(61.64, 137.5) * mm, v(63.95, 135.97) * mm, v(65.96, 134.48) * mm, v(67.64, 133.04) * mm, v(69.07, 131.62) * mm, v(70.73, 129.77) * mm, v(71.81, 128.37) * mm, v(72.55, 127.42) * mm]});
            skArc(sketch, "E49", {"start": v(-71.36, -40.3) * mm, "mid": v(-70.58, -40.8) * mm, "end": v(-70.13, -39.99) * mm});
            skArc(sketch, "E50", {"start": v(-75.91, -16.7) * mm, "mid": v(-76.67, -16.27) * mm, "end": v(-77.15, -17) * mm});
            skArc(sketch, "E51", {"start": v(-81.04, -11.63) * mm, "mid": v(-81.77, -11.15) * mm, "end": v(-82.28, -11.87) * mm});
            skArc(sketch, "E52", {"start": v(-128.58, 63.75) * mm, "mid": v(-128.2, 64.66) * mm, "end": v(-129.18, 64.87) * mm});
            skArc(sketch, "E53", {"start": v(-128.58, 71.52) * mm, "mid": v(-128.42, 72.42) * mm, "end": v(-129.32, 72.56) * mm});
            skArc(sketch, "E54", {"start": v(-148.77, 89.49) * mm, "mid": v(-147.99, 90.04) * mm, "end": v(-148.63, 90.75) * mm});
            skArc(sketch, "E55", {"start": v(-139.31, 93) * mm, "mid": v(-138.55, 93.47) * mm, "end": v(-139.02, 94.23) * mm});
            skArc(sketch, "E56", {"start": v(-48.59, 161.54) * mm, "mid": v(-47.83, 161.97) * mm, "end": v(-48.2, 162.75) * mm});
            skArc(sketch, "E57", {"start": v(-43.27, 157.65) * mm, "mid": v(-43.13, 158.49) * mm, "end": v(-43.94, 158.73) * mm});
            skArc(sketch, "E58", {"start": v(-94.1, 127.36) * mm, "mid": v(-93.83, 126.52) * mm, "end": v(-92.99, 126.76) * mm});
            skArc(sketch, "E59", {"start": v(-91.76, 118.58) * mm, "mid": v(-91.53, 117.72) * mm, "end": v(-90.67, 117.92) * mm});
            skArc(sketch, "E60", {"start": v(92.47, -5.11) * mm, "mid": v(92.15, -4.19) * mm, "end": v(91.3, -4.65) * mm});
            skArc(sketch, "E61", {"start": v(85.97, -35.34) * mm, "mid": v(86.58, -36.06) * mm, "end": v(87.24, -35.4) * mm});
            skArc(sketch, "E62", {"start": v(93.64, -24.36) * mm, "mid": v(92.9, -23.9) * mm, "end": v(92.39, -24.6) * mm});
            skArc(sketch, "E63", {"start": v(119.43, -14.87) * mm, "mid": v(118.62, -14.5) * mm, "end": v(118.23, -15.3) * mm});
            skArc(sketch, "E64", {"start": v(110.97, 3.6) * mm, "mid": v(110.34, 4.13) * mm, "end": v(109.7, 3.62) * mm});
            skArc(sketch, "E65", {"start": v(180.8, 52.76) * mm, "mid": v(180.61, 53.59) * mm, "end": v(179.77, 53.5) * mm});
            skArc(sketch, "E66", {"start": v(177.82, 58.36) * mm, "mid": v(178.56, 59) * mm, "end": v(177.8, 59.63) * mm});
            skArc(sketch, "E67", {"start": v(185.85, 75.64) * mm, "mid": v(185.89, 76.55) * mm, "end": v(184.97, 76.56) * mm});
            skArc(sketch, "E68", {"start": v(123.5, 74.83) * mm, "mid": v(122.51, 74.92) * mm, "end": v(122.6, 73.93) * mm});
            skArc(sketch, "E69", {"start": v(132.94, 76.02) * mm, "mid": v(131.98, 75.83) * mm, "end": v(132.32, 74.9) * mm});
            skArc(sketch, "E70", {"start": v(182.64, 101.38) * mm, "mid": v(183.43, 101.98) * mm, "end": v(182.69, 102.64) * mm});
            skArc(sketch, "E71", {"start": v(172.22, 114.8) * mm, "mid": v(172.34, 115.68) * mm, "end": v(171.49, 115.84) * mm});
            skArc(sketch, "E72", {"start": v(136.36, 94.86) * mm, "mid": v(135.67, 94.3) * mm, "end": v(136.22, 93.6) * mm});
            skArc(sketch, "E73", {"start": v(137.62, 102.33) * mm, "mid": v(137.34, 101.5) * mm, "end": v(138.16, 101.18) * mm});
            skArc(sketch, "E74", {"start": v(136.36, 152.33) * mm, "mid": v(137.3, 152.36) * mm, "end": v(137.2, 153.3) * mm});
            skArc(sketch, "E75", {"start": v(64.81, 144.24) * mm, "mid": v(65.68, 144.52) * mm, "end": v(65.37, 145.38) * mm});
            skArc(sketch, "E76", {"start": v(72.55, 127.42) * mm, "mid": v(73.5, 127.22) * mm, "end": v(73.55, 128.2) * mm});
            skArc(sketch, "E77", {"start": v(-100.97, -1.72) * mm, "mid": v(-101.7, -1.17) * mm, "end": v(-102.22, -1.94) * mm});
            skArc(sketch, "E78", {"start": v(-104.6, 6.3) * mm, "mid": v(-105.27, 7) * mm, "end": v(-105.88, 6.26) * mm});
            skSolve(sketch);
        }
        {
            var Q0;
            Q0 = qSketchRegion(id + "F6", true);
            extrude(context, id + "F7", {"entities" : qUnion([Q0]), "operationType" : NewBodyOperationType.REMOVE, "endBound" : BoundingType.THROUGH_ALL, "oppositeDirection" : true, "depth" : 25.4 * mm, "hasSecondDirection" : true, "secondDirectionOppositeDirection" : false, "secondDirectionDepth" : 25.4 * mm});
        }
    });
